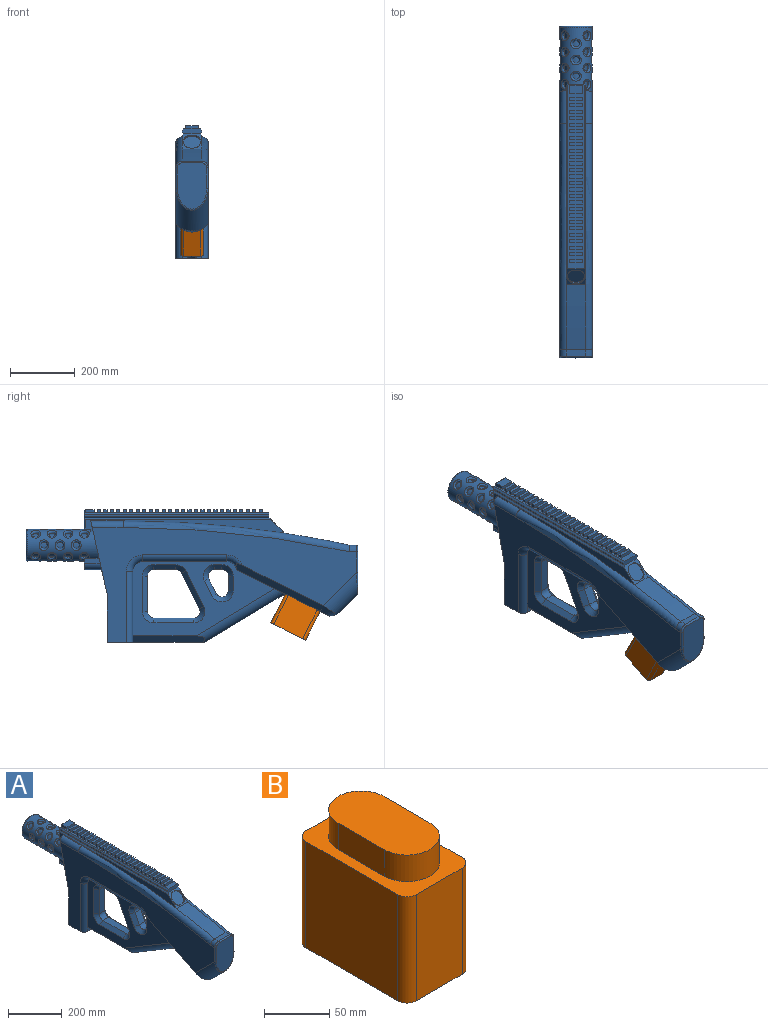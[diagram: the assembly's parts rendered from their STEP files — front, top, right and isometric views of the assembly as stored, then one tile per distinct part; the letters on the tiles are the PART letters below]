
ASSEMBLY  parts=2 mates=1
PART A: 340 faces, bbox 114x1061.1x421.4 mm
  f0: plane 168.93x84.47mm, normal (0,0.45,-0.89), area 4784.2mm2, adj f297,f298,f299,f300,f301,f303,f304,f307
  f1: plane 142.93x90mm, normal (0,-1,0), area 11537.9mm2, adj f308,f309,f310,f311,f312,f313
  f2: plane 60x47.7mm, normal (0,-0.71,0.71), area 1586.1mm2, adj f7,f8,f79,f80,f81,f82,f287,f288
  f3: plane 76.87x21.87mm, normal (0,0.98,-0.22), area 875.9mm2, adj f8,f13,f47,f225
  f4: plane 151.87x101.87mm, normal (0,0.98,-0.22), area 9786.5mm2, adj f9,f12,f13,f32,f33,f34,f87,f88
  f5: plane 567.11x50mm, normal (0,0,1), area 16871.1mm2, adj f82,f89,f90,f91,f92,f93,f94,f96
  f6: plane 60x20mm, normal (0,0,1), area 1200mm2, adj f44,f45,f79,f308
  f7: plane 614.81x42.7mm, normal (-1,0,0), area 8968mm2, adj f2,f15,f46,f48,f80,f225,f319,f325
  f8: plane 614.81x42.7mm, normal (1,0,0), area 8968mm2, adj f2,f3,f43,f47,f81,f225,f319,f320
  f9: plane 150x100mm, normal (0,1,0), area 15000mm2, adj f4,f12,f13,f14
  f10: plane 20x20mm, normal (0,-1,0), area 200mm2, adj f14,f38,f50
  f11: plane 20x20mm, normal (0,-1,0), area 200mm2, adj f14,f42,f49
  f12: plane 815.56x355mm, normal (-1,0,0), area 102541.9mm2, adj f4,f9,f14,f15,f39,f40,f41,f42
  f13: plane 815.56x355mm, normal (1,0,0), area 102541.9mm2, adj f3,f4,f9,f14,f35,f36,f37,f38
  f14: plane 305.72x105.72mm, normal (0,0,-1), area 12206.3mm2, adj f9,f10,f11,f12,f13,f38,f42,f49
  f15: plane 76.87x21.87mm, normal (0,0.98,-0.22), area 875.9mm2, adj f7,f12,f48,f225
  f16: plane 45.28x30mm, normal (0,-0.89,0.45), area 1518.7mm2, adj f25,f27,f71,f73
  f17: plane 45.28x30mm, normal (0,1,0), area 1358.4mm2, adj f25,f30,f70,f76
  f18: plane 122.64x30mm, normal (0,0,1), area 3679.2mm2, adj f26,f29,f58,f63
  f19: plane 110x55mm, normal (0,0.89,-0.45), area 3689.5mm2, adj f26,f31,f54,f59
  f20: plane 67.64x30mm, normal (0,0,-1), area 2029.2mm2, adj f28,f31,f51,f62
  f21: plane 30x22.64mm, normal (0,0,-1), area 679.2mm2, adj f27,f30,f67,f77
  f22: plane 110x30mm, normal (0,-1,0), area 3300mm2, adj f28,f29,f55,f66
  f23: plane 438.2x230mm, normal (1,0,0), area 38584.8mm2, adj f35,f36,f37,f38,f50,f59,f60,f61
  f24: plane 438.2x230mm, normal (-1,0,0), area 38584.8mm2, adj f39,f40,f41,f42,f49,f51,f52,f53
  f25: cylinder r=20mm len=37.89mm, axis (-1,0,0), area 1606.8mm2, adj f16,f17,f72,f74
  f26: cylinder r=20mm len=30mm, axis (1,0,0), area 1220.7mm2, adj f18,f19,f56,f61
  f27: cylinder r=20mm len=30mm, axis (1,0,0), area 1220.7mm2, adj f16,f21,f69,f75
  f28: cylinder r=20mm len=30mm, axis (1,0,0), area 942.5mm2, adj f20,f22,f53,f64
  f29: cylinder r=20mm len=30mm, axis (-1,0,0), area 942.5mm2, adj f18,f22,f57,f65
  f30: cylinder r=20mm len=30mm, axis (-1,0,0), area 942.5mm2, adj f17,f21,f68,f78
  f31: cylinder r=20mm len=30mm, axis (-1,0,0), area 664.3mm2, adj f19,f20,f52,f60
  f32: plane 48.89x15mm, normal (1,0,0), area 708.3mm2, adj f4,f87,f225,f316,f317
  f33: plane 48.89x15mm, normal (-1,0,0), area 708.3mm2, adj f4,f88,f225,f315,f317
  f34: plane 53.33x20mm, normal (0,0,-1), area 1066.7mm2, adj f4,f87,f88,f317
  f35: torus R=50mm, axis (1,0,0), area 1252mm2, adj f13,f23,f36,f297
  f36: cylinder r=20mm len=260.42mm, axis (0,-1,0), area 8181.3mm2, adj f13,f23,f35,f37
  f37: torus R=50mm, axis (1,0,0), area 1839.1mm2, adj f13,f23,f36,f38
  f38: cylinder r=20mm len=220mm, axis (0,0,1), area 6911.5mm2, adj f10,f13,f14,f23,f37
  f39: torus R=50mm, axis (1,0,0), area 1252.2mm2, adj f12,f24,f40,f299
  f40: cylinder r=20mm len=260.42mm, axis (0,1,0), area 8181.3mm2, adj f12,f24,f39,f41
  f41: torus R=50mm, axis (1,0,0), area 1839.1mm2, adj f12,f24,f40,f42
  f42: cylinder r=20mm len=220mm, axis (0,0,-1), area 6911.5mm2, adj f11,f12,f14,f24,f41
  f43: torus R=3284.17mm, axis (1,0,0), area 22144mm2, adj f8,f13,f44,f47,f79
  f44: cylinder r=20mm len=22.15mm, axis (0,1,0), area 662mm2, adj f6,f13,f43,f310
  f45: cylinder r=20mm len=22.15mm, axis (0,-1,0), area 662mm2, adj f6,f12,f46,f309
  f46: torus R=3284.17mm, axis (1,0,0), area 22144mm2, adj f7,f12,f45,f48,f79
  f47: cylinder r=20mm len=100mm, axis (0,-1,0), area 3071.8mm2, adj f3,f8,f13,f43
  f48: cylinder r=20mm len=100mm, axis (0,-1,0), area 3071.8mm2, adj f7,f12,f15,f46
  f49: plane 221.84x20mm, normal (-0.71,0,-0.71), area 6178.6mm2, adj f11,f14,f24,f307
  f50: plane 221.84x20mm, normal (0.71,0,-0.71), area 6178.6mm2, adj f10,f14,f23,f307
  f51: plane 67.64x15mm, normal (-0.71,0,-0.71), area 1434.8mm2, adj f20,f24,f52,f53
  f52: cone r=35mm half-angle=45deg, axis (-1,0,0), area 645.9mm2, adj f24,f31,f51,f54
  f53: cone r=35mm half-angle=45deg, axis (-1,0,0), area 916.3mm2, adj f24,f28,f51,f55
  f54: plane 116.71x68.42mm, normal (-0.71,0.63,-0.32), area 2608.9mm2, adj f19,f24,f52,f56
  f55: plane 110x15mm, normal (-0.71,-0.71,0), area 2333.5mm2, adj f22,f24,f53,f57
  f56: cone r=35mm half-angle=45deg, axis (-1,0,0), area 1186.8mm2, adj f24,f26,f54,f58
  f57: cone r=35mm half-angle=45deg, axis (-1,0,0), area 916.3mm2, adj f24,f29,f55,f58
  f58: plane 122.64x15mm, normal (-0.71,0,0.71), area 2601.6mm2, adj f18,f24,f56,f57
  f59: plane 116.71x68.42mm, normal (0.71,0.63,-0.32), area 2608.9mm2, adj f19,f23,f60,f61
  f60: cone r=35mm half-angle=45deg, axis (1,0,0), area 645.9mm2, adj f23,f31,f59,f62
  f61: cone r=35mm half-angle=45deg, axis (1,0,0), area 1186.8mm2, adj f23,f26,f59,f63
  f62: plane 67.64x15mm, normal (0.71,0,-0.71), area 1434.8mm2, adj f20,f23,f60,f64
  f63: plane 122.64x15mm, normal (0.71,0,0.71), area 2601.6mm2, adj f18,f23,f61,f65
  f64: cone r=35mm half-angle=45deg, axis (1,0,0), area 916.3mm2, adj f23,f28,f62,f66
  f65: cone r=35mm half-angle=45deg, axis (1,0,0), area 916.3mm2, adj f23,f29,f63,f66
  f66: plane 110x15mm, normal (0.71,-0.71,0), area 2333.5mm2, adj f22,f23,f64,f65
  f67: plane 22.64x15mm, normal (-0.71,0,-0.71), area 480.3mm2, adj f21,f24,f68,f69
  f68: cone r=35mm half-angle=45deg, axis (-1,0,0), area 916.3mm2, adj f24,f30,f67,f70
  f69: cone r=35mm half-angle=45deg, axis (-1,0,0), area 1186.8mm2, adj f24,f27,f67,f71
  f70: plane 45.28x15mm, normal (-0.71,0.71,0), area 960.5mm2, adj f17,f24,f68,f72
  f71: plane 51.99x36.06mm, normal (-0.71,-0.63,0.32), area 1073.9mm2, adj f16,f24,f69,f72
  f72: cone r=35mm half-angle=45deg, axis (-1,0,0), area 1562.2mm2, adj f24,f25,f70,f71
  f73: plane 51.99x36.06mm, normal (0.71,-0.63,0.32), area 1073.9mm2, adj f16,f23,f74,f75
  f74: cone r=35mm half-angle=45deg, axis (1,0,0), area 1562.2mm2, adj f23,f25,f73,f76
  f75: cone r=35mm half-angle=45deg, axis (1,0,0), area 1186.8mm2, adj f23,f27,f73,f77
  f76: plane 45.28x15mm, normal (0.71,0.71,0), area 960.5mm2, adj f17,f23,f74,f78
  f77: plane 22.64x15mm, normal (0.71,0,-0.71), area 480.3mm2, adj f21,f23,f75,f78
  f78: cone r=35mm half-angle=45deg, axis (1,0,0), area 916.3mm2, adj f23,f30,f76,f77
  f79: cylinder r=3304.17mm len=202.3mm, axis (-1,0,0), area 12344.7mm2, adj f2,f6,f43,f46
  f80: plane 572.11x5mm, normal (-0.71,0,0.71), area 4027.8mm2, adj f2,f7,f86,f332
  f81: plane 572.11x5mm, normal (0.71,0,0.71), area 4027.8mm2, adj f2,f8,f85,f322
  f82: plane 60x15mm, normal (0,-1,0), area 850mm2, adj f2,f5,f83,f84,f85,f86,f89,f90
  f83: plane 567.11x5mm, normal (1,0,0), area 2835.6mm2, adj f82,f85,f90,f327
  f84: plane 567.11x5mm, normal (-1,0,0), area 2835.6mm2, adj f82,f86,f89,f336
  f85: plane 567.11x5mm, normal (0.71,0,-0.71), area 4010.1mm2, adj f81,f82,f83,f324
  f86: plane 567.11x5mm, normal (-0.71,0,-0.71), area 4010.1mm2, adj f80,f82,f84,f334
  f87: cylinder r=20mm len=53.33mm, axis (0,-1,0), area 1605.7mm2, adj f4,f32,f34,f317
  f88: cylinder r=20mm len=53.33mm, axis (0,1,0), area 1605.7mm2, adj f4,f33,f34,f317
  f89: plane 567.11x5mm, normal (-0.71,0,0.71), area 4010.1mm2, adj f5,f82,f84,f338
  f90: plane 567.11x5mm, normal (0.71,0,0.71), area 4010.1mm2, adj f5,f82,f83,f329
  f91: plane 40x10mm, normal (0,-1,0), area 400mm2, adj f5,f92,f94,f95
  f92: plane 10x10mm, normal (1,0,0), area 100mm2, adj f5,f91,f93,f95
  f93: plane 40x10mm, normal (0,1,0), area 400mm2, adj f5,f92,f94,f95
  f94: plane 10x10mm, normal (-1,0,0), area 100mm2, adj f5,f91,f93,f95
  f95: plane 40x10mm, normal (0,0,1), area 400mm2, adj f91,f92,f93,f94
  f96: plane 10x10mm, normal (-1,0,0), area 100mm2, adj f5,f97,f99,f100
  f97: plane 40x10mm, normal (0,-1,0), area 400mm2, adj f5,f96,f98,f100
  f98: plane 10x10mm, normal (1,0,0), area 100mm2, adj f5,f97,f99,f100
  f99: plane 40x10mm, normal (0,1,0), area 400mm2, adj f5,f96,f98,f100
  f100: plane 40x10mm, normal (0,0,1), area 400mm2, adj f96,f97,f98,f99
  f101: plane 40x10mm, normal (0,-1,0), area 400mm2, adj f5,f102,f104,f105
  f102: plane 10x10mm, normal (1,0,0), area 100mm2, adj f5,f101,f103,f105
  f103: plane 40x10mm, normal (0,1,0), area 400mm2, adj f5,f102,f104,f105
  f104: plane 10x10mm, normal (-1,0,0), area 100mm2, adj f5,f101,f103,f105
  f105: plane 40x10mm, normal (0,0,1), area 400mm2, adj f101,f102,f103,f104
  f106: plane 40x10mm, normal (0,-1,0), area 400mm2, adj f5,f107,f109,f110
  f107: plane 10x10mm, normal (1,0,0), area 100mm2, adj f5,f106,f108,f110
  f108: plane 40x10mm, normal (0,1,0), area 400mm2, adj f5,f107,f109,f110
  f109: plane 10x10mm, normal (-1,0,0), area 100mm2, adj f5,f106,f108,f110
  f110: plane 40x10mm, normal (0,0,1), area 400mm2, adj f106,f107,f108,f109
  f111: plane 40x10mm, normal (0,-1,0), area 400mm2, adj f5,f112,f114,f115
  f112: plane 10x10mm, normal (1,0,0), area 100mm2, adj f5,f111,f113,f115
  f113: plane 40x10mm, normal (0,1,0), area 400mm2, adj f5,f112,f114,f115
  f114: plane 10x10mm, normal (-1,0,0), area 100mm2, adj f5,f111,f113,f115
  f115: plane 40x10mm, normal (0,0,1), area 400mm2, adj f111,f112,f113,f114
  f116: plane 40x10mm, normal (0,-1,0), area 400mm2, adj f5,f117,f119,f120
  f117: plane 10x10mm, normal (1,0,0), area 100mm2, adj f5,f116,f118,f120
  f118: plane 40x10mm, normal (0,1,0), area 400mm2, adj f5,f117,f119,f120
  f119: plane 10x10mm, normal (-1,0,0), area 100mm2, adj f5,f116,f118,f120
  f120: plane 40x10mm, normal (0,0,1), area 400mm2, adj f116,f117,f118,f119
  f121: plane 10x10mm, normal (-1,0,0), area 100mm2, adj f5,f122,f124,f125
  f122: plane 40x10mm, normal (0,-1,0), area 400mm2, adj f5,f121,f123,f125
  f123: plane 10x10mm, normal (1,0,0), area 100mm2, adj f5,f122,f124,f125
  f124: plane 40x10mm, normal (0,1,0), area 400mm2, adj f5,f121,f123,f125
  f125: plane 40x10mm, normal (0,0,1), area 400mm2, adj f121,f122,f123,f124
  f126: plane 40x10mm, normal (0,-1,0), area 400mm2, adj f5,f127,f129,f130
  f127: plane 10x10mm, normal (1,0,0), area 100mm2, adj f5,f126,f128,f130
  f128: plane 40x10mm, normal (0,1,0), area 400mm2, adj f5,f127,f129,f130
  f129: plane 10x10mm, normal (-1,0,0), area 100mm2, adj f5,f126,f128,f130
  f130: plane 40x10mm, normal (0,0,1), area 400mm2, adj f126,f127,f128,f129
  f131: plane 40x10mm, normal (0,-1,0), area 400mm2, adj f5,f132,f134,f135
  f132: plane 10x10mm, normal (1,0,0), area 100mm2, adj f5,f131,f133,f135
  f133: plane 40x10mm, normal (0,1,0), area 400mm2, adj f5,f132,f134,f135
  f134: plane 10x10mm, normal (-1,0,0), area 100mm2, adj f5,f131,f133,f135
  f135: plane 40x10mm, normal (0,0,1), area 400mm2, adj f131,f132,f133,f134
  f136: plane 40x10mm, normal (0,-1,0), area 400mm2, adj f5,f137,f139,f140
  f137: plane 10x10mm, normal (1,0,0), area 100mm2, adj f5,f136,f138,f140
  f138: plane 40x10mm, normal (0,1,0), area 400mm2, adj f5,f137,f139,f140
  f139: plane 10x10mm, normal (-1,0,0), area 100mm2, adj f5,f136,f138,f140
  f140: plane 40x10mm, normal (0,0,1), area 400mm2, adj f136,f137,f138,f139
  f141: plane 10x10mm, normal (-1,0,0), area 100mm2, adj f5,f142,f144,f145
  f142: plane 40x10mm, normal (0,-1,0), area 400mm2, adj f5,f141,f143,f145
  f143: plane 10x10mm, normal (1,0,0), area 100mm2, adj f5,f142,f144,f145
  f144: plane 40x10mm, normal (0,1,0), area 400mm2, adj f5,f141,f143,f145
  f145: plane 40x10mm, normal (0,0,1), area 400mm2, adj f141,f142,f143,f144
  f146: plane 40x10mm, normal (0,-1,0), area 400mm2, adj f5,f147,f149,f150
  f147: plane 10x10mm, normal (1,0,0), area 100mm2, adj f5,f146,f148,f150
  f148: plane 40x10mm, normal (0,1,0), area 400mm2, adj f5,f147,f149,f150
  f149: plane 10x10mm, normal (-1,0,0), area 100mm2, adj f5,f146,f148,f150
  f150: plane 40x10mm, normal (0,0,1), area 400mm2, adj f146,f147,f148,f149
  f151: plane 10x10mm, normal (-1,0,0), area 100mm2, adj f5,f152,f154,f155
  f152: plane 40x10mm, normal (0,-1,0), area 400mm2, adj f5,f151,f153,f155
  f153: plane 10x10mm, normal (1,0,0), area 100mm2, adj f5,f152,f154,f155
  f154: plane 40x10mm, normal (0,1,0), area 400mm2, adj f5,f151,f153,f155
  f155: plane 40x10mm, normal (0,0,1), area 400mm2, adj f151,f152,f153,f154
  f156: plane 10x10mm, normal (-1,0,0), area 100mm2, adj f5,f157,f159,f160
  f157: plane 40x10mm, normal (0,-1,0), area 400mm2, adj f5,f156,f158,f160
  f158: plane 10x10mm, normal (1,0,0), area 100mm2, adj f5,f157,f159,f160
  f159: plane 40x10mm, normal (0,1,0), area 400mm2, adj f5,f156,f158,f160
  f160: plane 40x10mm, normal (0,0,1), area 400mm2, adj f156,f157,f158,f159
  f161: plane 10x10mm, normal (-1,0,0), area 100mm2, adj f5,f162,f164,f165
  f162: plane 40x10mm, normal (0,-1,0), area 400mm2, adj f5,f161,f163,f165
  f163: plane 10x10mm, normal (1,0,0), area 100mm2, adj f5,f162,f164,f165
  f164: plane 40x10mm, normal (0,1,0), area 400mm2, adj f5,f161,f163,f165
  f165: plane 40x10mm, normal (0,0,1), area 400mm2, adj f161,f162,f163,f164
  f166: plane 10x10mm, normal (-1,0,0), area 100mm2, adj f5,f167,f169,f170
  f167: plane 40x10mm, normal (0,-1,0), area 400mm2, adj f5,f166,f168,f170
  f168: plane 10x10mm, normal (1,0,0), area 100mm2, adj f5,f167,f169,f170
  f169: plane 40x10mm, normal (0,1,0), area 400mm2, adj f5,f166,f168,f170
  f170: plane 40x10mm, normal (0,0,1), area 400mm2, adj f166,f167,f168,f169
  f171: plane 10x10mm, normal (-1,0,0), area 100mm2, adj f5,f172,f174,f175
  f172: plane 40x10mm, normal (0,-1,0), area 400mm2, adj f5,f171,f173,f175
  f173: plane 10x10mm, normal (1,0,0), area 100mm2, adj f5,f172,f174,f175
  f174: plane 40x10mm, normal (0,1,0), area 400mm2, adj f5,f171,f173,f175
  f175: plane 40x10mm, normal (0,0,1), area 400mm2, adj f171,f172,f173,f174
  f176: plane 10x10mm, normal (-1,0,0), area 100mm2, adj f5,f177,f179,f180
  f177: plane 40x10mm, normal (0,-1,0), area 400mm2, adj f5,f176,f178,f180
  f178: plane 10x10mm, normal (1,0,0), area 100mm2, adj f5,f177,f179,f180
  f179: plane 40x10mm, normal (0,1,0), area 400mm2, adj f5,f176,f178,f180
  f180: plane 40x10mm, normal (0,0,1), area 400mm2, adj f176,f177,f178,f179
  f181: plane 10x10mm, normal (-1,0,0), area 100mm2, adj f5,f182,f184,f185
  f182: plane 40x10mm, normal (0,-1,0), area 400mm2, adj f5,f181,f183,f185
  f183: plane 10x10mm, normal (1,0,0), area 100mm2, adj f5,f182,f184,f185
  f184: plane 40x10mm, normal (0,1,0), area 400mm2, adj f5,f181,f183,f185
  f185: plane 40x10mm, normal (0,0,1), area 400mm2, adj f181,f182,f183,f184
  f186: plane 10x10mm, normal (-1,0,0), area 100mm2, adj f5,f187,f189,f190
  f187: plane 40x10mm, normal (0,-1,0), area 400mm2, adj f5,f186,f188,f190
  f188: plane 10x10mm, normal (1,0,0), area 100mm2, adj f5,f187,f189,f190
  f189: plane 40x10mm, normal (0,1,0), area 400mm2, adj f5,f186,f188,f190
  f190: plane 40x10mm, normal (0,0,1), area 400mm2, adj f186,f187,f188,f189
  f191: plane 10x10mm, normal (-1,0,0), area 100mm2, adj f5,f192,f194,f195
  f192: plane 40x10mm, normal (0,-1,0), area 400mm2, adj f5,f191,f193,f195
  f193: plane 10x10mm, normal (1,0,0), area 100mm2, adj f5,f192,f194,f195
  f194: plane 40x10mm, normal (0,1,0), area 400mm2, adj f5,f191,f193,f195
  f195: plane 40x10mm, normal (0,0,1), area 400mm2, adj f191,f192,f193,f194
  f196: plane 10x10mm, normal (-1,0,0), area 100mm2, adj f5,f197,f199,f200
  f197: plane 40x10mm, normal (0,-1,0), area 400mm2, adj f5,f196,f198,f200
  f198: plane 10x10mm, normal (1,0,0), area 100mm2, adj f5,f197,f199,f200
  f199: plane 40x10mm, normal (0,1,0), area 400mm2, adj f5,f196,f198,f200
  f200: plane 40x10mm, normal (0,0,1), area 400mm2, adj f196,f197,f198,f199
  f201: plane 10x10mm, normal (-1,0,0), area 100mm2, adj f5,f202,f204,f205
  f202: plane 40x10mm, normal (0,-1,0), area 400mm2, adj f5,f201,f203,f205
  f203: plane 10x10mm, normal (1,0,0), area 100mm2, adj f5,f202,f204,f205
  f204: plane 40x10mm, normal (0,1,0), area 400mm2, adj f5,f201,f203,f205
  f205: plane 40x10mm, normal (0,0,1), area 400mm2, adj f201,f202,f203,f204
  f206: plane 10x10mm, normal (-1,0,0), area 100mm2, adj f5,f207,f209,f210
  f207: plane 40x10mm, normal (0,-1,0), area 400mm2, adj f5,f206,f208,f210
  f208: plane 10x10mm, normal (1,0,0), area 100mm2, adj f5,f207,f209,f210
  f209: plane 40x10mm, normal (0,1,0), area 400mm2, adj f5,f206,f208,f210
  f210: plane 40x10mm, normal (0,0,1), area 400mm2, adj f206,f207,f208,f209
  f211: plane 10x10mm, normal (-1,0,0), area 100mm2, adj f5,f212,f214,f215
  f212: plane 40x10mm, normal (0,-1,0), area 400mm2, adj f5,f211,f213,f215
  f213: plane 10x10mm, normal (1,0,0), area 100mm2, adj f5,f212,f214,f215
  f214: plane 40x10mm, normal (0,1,0), area 400mm2, adj f5,f211,f213,f215
  f215: plane 40x10mm, normal (0,0,1), area 400mm2, adj f211,f212,f213,f214
  f216: plane 40x10mm, normal (0,-1,0), area 400mm2, adj f5,f217,f218,f219
  f217: plane 27.11x10mm, normal (1,0,0), area 271.1mm2, adj f5,f216,f219,f333
  f218: plane 27.11x10mm, normal (-1,0,0), area 271.1mm2, adj f5,f216,f219,f337
  f219: plane 40x27.11mm, normal (0,0,1), area 1084.5mm2, adj f216,f217,f218,f335
  f220: plane 10x10mm, normal (1,0,0), area 100mm2, adj f5,f221,f223,f224
  f221: plane 40x10mm, normal (0,1,0), area 400mm2, adj f5,f220,f222,f224
  f222: plane 10x10mm, normal (-1,0,0), area 100mm2, adj f5,f221,f223,f224
  f223: plane 40x10mm, normal (0,-1,0), area 400mm2, adj f5,f220,f222,f224
  f224: plane 40x10mm, normal (0,0,1), area 400mm2, adj f220,f221,f222,f223
  f225: cylinder r=50mm len=220.56mm, axis (0,1,0), area 40915mm2, adj f3,f4,f7,f8,f15,f32,f33,f228
  f226: cylinder r=40mm len=195mm, axis (0,1,0), area 31299.6mm2, adj f227,f229,f231,f233,f235,f237,f239,f241
  f227: plane 80x80mm, normal (0,1,0), area 1178.1mm2, adj f226,f285
  f228: bspline ~30.01x23.58mm, area 668.6mm2, adj f225,f229
  f229: bspline ~29.98x19.83mm, area 508.6mm2, adj f226,f228
  f230: bspline ~30.01x23.58mm, area 668.6mm2, adj f225,f231
  f231: bspline ~29.98x19.83mm, area 508.6mm2, adj f226,f230
  f232: bspline ~30.01x23.58mm, area 668.6mm2, adj f225,f233
  f233: bspline ~29.98x19.83mm, area 508.6mm2, adj f226,f232
  f234: bspline ~30.01x23.58mm, area 668.6mm2, adj f225,f235
  f235: bspline ~29.98x19.83mm, area 508.6mm2, adj f226,f234
  f236: bspline ~33.35x30.01mm, area 668.6mm2, adj f225,f237
  f237: bspline ~29.98x26.65mm, area 508.6mm2, adj f226,f236
  f238: bspline ~33.35x30.01mm, area 668.6mm2, adj f225,f239
  f239: bspline ~29.98x26.65mm, area 508.6mm2, adj f226,f238
  f240: bspline ~33.35x30.01mm, area 668.6mm2, adj f225,f241
  f241: bspline ~29.98x26.65mm, area 508.6mm2, adj f226,f240
  f242: bspline ~33.35x30.01mm, area 668.8mm2, adj f225,f243
  f243: bspline ~29.98x26.65mm, area 508.6mm2, adj f226,f242
  f244: bspline ~33.35x30.01mm, area 668.8mm2, adj f225,f245
  f245: bspline ~29.98x26.65mm, area 508.6mm2, adj f226,f244
  f246: bspline ~33.35x30.01mm, area 668.8mm2, adj f225,f247
  f247: bspline ~29.98x26.65mm, area 508.6mm2, adj f226,f246
  f248: bspline ~33.35x30.01mm, area 668.6mm2, adj f225,f249
  f249: bspline ~29.98x26.65mm, area 508.6mm2, adj f226,f248
  f250: bspline ~33.35x30.01mm, area 668.6mm2, adj f225,f251
  f251: bspline ~29.98x26.65mm, area 508.6mm2, adj f226,f250
  f252: bspline ~33.35x30.01mm, area 668.6mm2, adj f225,f253
  f253: bspline ~29.98x26.65mm, area 508.6mm2, adj f226,f252
  f254: bspline ~33.35x30.01mm, area 668.6mm2, adj f225,f255
  f255: bspline ~29.98x26.65mm, area 508.6mm2, adj f226,f254
  f256: bspline ~33.35x30.01mm, area 668.6mm2, adj f225,f257
  f257: bspline ~29.98x26.65mm, area 508.6mm2, adj f226,f256
  f258: bspline ~33.35x30.01mm, area 668.6mm2, adj f225,f259
  f259: bspline ~29.98x26.65mm, area 508.6mm2, adj f226,f258
  f260: bspline ~30.01x23.58mm, area 668.6mm2, adj f225,f261
  f261: bspline ~29.98x19.83mm, area 508.6mm2, adj f226,f260
  f262: bspline ~30.01x23.58mm, area 668.6mm2, adj f225,f263
  f263: bspline ~29.98x19.83mm, area 508.6mm2, adj f226,f262
  f264: bspline ~30.01x23.58mm, area 668.6mm2, adj f225,f265
  f265: bspline ~29.98x19.83mm, area 508.6mm2, adj f226,f264
  f266: bspline ~30.01x23.58mm, area 668.6mm2, adj f225,f267,f316
  f267: bspline ~29.98x19.83mm, area 508.6mm2, adj f226,f266
  f268: bspline ~30.04x23.59mm, area 668.8mm2, adj f225,f269
  f269: bspline ~29.98x19.83mm, area 508.7mm2, adj f226,f268
  f270: bspline ~30.04x23.59mm, area 668.8mm2, adj f225,f271
  f271: bspline ~29.98x19.83mm, area 508.7mm2, adj f226,f270
  f272: bspline ~30.04x23.59mm, area 668.8mm2, adj f225,f273
  f273: bspline ~29.98x19.83mm, area 508.7mm2, adj f226,f272
  f274: bspline ~30.04x23.59mm, area 668.8mm2, adj f225,f275,f315
  f275: bspline ~29.98x19.83mm, area 508.7mm2, adj f226,f274
  f276: bspline ~30.04x23.59mm, area 668.8mm2, adj f225,f277
  f277: bspline ~29.98x19.83mm, area 508.7mm2, adj f226,f276
  f278: bspline ~30.04x23.59mm, area 668.8mm2, adj f225,f279
  f279: bspline ~29.98x19.83mm, area 508.7mm2, adj f226,f278
  f280: bspline ~30.04x23.59mm, area 668.8mm2, adj f225,f281
  f281: bspline ~29.98x19.83mm, area 508.7mm2, adj f226,f280
  f282: bspline ~30.04x23.59mm, area 668.8mm2, adj f225,f283
  f283: bspline ~29.98x19.83mm, area 508.7mm2, adj f226,f282
  f284: torus R=45mm, axis (0,1,0), area 4441.3mm2, adj f225,f226
  f285: cylinder r=35mm len=190mm, axis (0,-1,0), area 41783.2mm2, adj f227,f286
  f286: plane 70x70mm, normal (0,1,0), area 2591.8mm2, adj f285,f305
  f287: plane 10x3.54mm, normal (0,-0.71,-0.71), area 50mm2, adj f2,f291,f292,f295
  f288: plane 14.41x14.41mm, normal (1,0,0), area 76.9mm2, adj f2,f291,f292,f293
  f289: plane 10x3.54mm, normal (0,0.71,0.71), area 50mm2, adj f2,f291,f293,f294
  f290: plane 14.41x14.41mm, normal (-1,0,0), area 76.9mm2, adj f2,f291,f294,f295
  f291: plane 50x39.16mm, normal (0,-0.71,0.71), area 2425.9mm2, adj f287,f288,f289,f290,f292,f293,f294,f295
  f292: cylinder r=20mm len=20mm, axis (0,-0.71,0.71), area 157.1mm2, adj f2,f287,f288,f291
  f293: cylinder r=20mm len=20mm, axis (0,0.71,-0.71), area 157.1mm2, adj f2,f288,f289,f291
  f294: cylinder r=20mm len=20mm, axis (0,-0.71,0.71), area 157.1mm2, adj f2,f289,f290,f291
  f295: cylinder r=20mm len=20mm, axis (0,0.71,-0.71), area 157.1mm2, adj f2,f287,f290,f291
  f296: cylinder r=50mm len=137.59mm, axis (0,0.71,-0.71), area 18210.5mm2, adj f12,f13,f298,f313
  f297: plane 269.45x147.11mm, normal (0.71,0.32,-0.63), area 8313.4mm2, adj f0,f13,f23,f35,f298
  f298: bspline ~100.01x51.37mm, area 3219.1mm2, adj f0,f296,f297,f299
  f299: plane 269.45x147.11mm, normal (-0.71,0.32,-0.63), area 8314.7mm2, adj f0,f12,f24,f39,f298
  f300: plane 55.9x44.72mm, normal (1,0,0), area 1250mm2, adj f0,f302,f303,f304
  f301: plane 55.9x44.72mm, normal (-1,0,0), area 1250mm2, adj f0,f302,f303,f304
  f302: plane 89.44x50mm, normal (0,0.45,-0.89), area 4463.5mm2, adj f300,f301,f303,f304
  f303: cylinder r=25mm len=50mm, axis (0,0.45,-0.89), area 1963.5mm2, adj f0,f300,f301,f302
  f304: cylinder r=25mm len=50mm, axis (0,0.45,-0.89), area 1963.5mm2, adj f0,f300,f301,f302
  f305: cylinder r=20mm len=175mm, axis (0,1,0), area 21991.1mm2, adj f286,f306
  f306: plane 40x40mm, normal (0,1,0), area 1256.6mm2, adj f305
  f307: cylinder r=30mm len=275.03mm, axis (0,0.86,-0.51), area 26712.1mm2, adj f0,f14,f23,f24,f49,f50
  f308: cylinder r=5mm len=60mm, axis (1,0,0), area 471.2mm2, adj f1,f6,f309,f310
  f309: torus R=15mm, axis (0,1,0), area 224.3mm2, adj f1,f45,f308,f311
  f310: torus R=15mm, axis (0,1,0), area 224.3mm2, adj f1,f44,f308,f312
  f311: cylinder r=5mm len=64.29mm, axis (0,0,-1), area 504.9mm2, adj f1,f12,f309,f313
  f312: cylinder r=5mm len=64.29mm, axis (0,0,1), area 504.9mm2, adj f1,f13,f310,f313
  f313: bspline ~100x67.14mm, area 1000.4mm2, adj f1,f296,f311,f312
  f314: plane 57.21x54.23mm, normal (0,1,0), area 2590.4mm2, adj f321,f322,f324,f326,f327,f329,f330,f331
  f315: cylinder r=50mm len=13.58mm, axis (0,-1,0), area 96.1mm2, adj f33,f274,f317
  f316: cylinder r=50mm len=13.58mm, axis (0,-1,0), area 67.2mm2, adj f32,f266,f317
  f317: plane 60x35mm, normal (0,1,0), area 1519.6mm2, adj f32,f33,f34,f87,f88,f225,f315,f316
  f318: cylinder r=60mm len=51.74mm, axis (0,1,0), area 915.4mm2, adj f319,f320,f325,f326
  f319: plane 60x13.16mm, normal (0,1,0), area 243.9mm2, adj f7,f8,f225,f318,f320,f325
  f320: plane 17.11x4.13mm, normal (0.53,0,-0.85), area 83.6mm2, adj f8,f318,f319,f323
  f321: plane 30.1x2.89mm, normal (0.71,0.71,0), area 120.4mm2, adj f8,f314,f322,f323
  f322: plane 9.08x6.2mm, normal (0.5,0.71,0.5), area 32.3mm2, adj f81,f314,f321,f324
  f323: plane 4.13x2.89mm, normal (0.47,0.47,-0.75), area 8mm2, adj f320,f321,f326
  f324: plane 9.08x6.2mm, normal (0.5,0.71,-0.5), area 32.3mm2, adj f85,f314,f322,f327
  f325: plane 17.11x4.13mm, normal (-0.53,0,-0.85), area 83.6mm2, adj f7,f318,f319,f328
  f326: cone r=60mm half-angle=45deg, axis (0,1,0), area 223.6mm2, adj f314,f318,f323,f328
  f327: plane 5x2.89mm, normal (0.71,0.71,0), area 15.5mm2, adj f83,f314,f324,f329
  f328: plane 4.13x2.89mm, normal (-0.47,0.47,-0.75), area 8mm2, adj f325,f326,f330
  f329: plane 6.2x6.2mm, normal (0.5,0.71,0.5), area 24mm2, adj f90,f314,f327,f331
  f330: plane 30.1x2.89mm, normal (-0.71,0.71,0), area 120.4mm2, adj f7,f314,f328,f332
  f331: plane 7.89x2.89mm, normal (0,0.71,0.71), area 23.9mm2, adj f5,f314,f329,f333
  f332: plane 9.08x6.2mm, normal (-0.5,0.71,0.5), area 32.3mm2, adj f80,f314,f330,f334
  f333: plane 12.89x2.89mm, normal (0.71,0.71,0), area 40.8mm2, adj f217,f314,f331,f335
  f334: plane 9.08x6.2mm, normal (-0.5,0.71,-0.5), area 32.3mm2, adj f86,f314,f332,f336
  f335: plane 40x2.89mm, normal (0,0.71,0.71), area 151.5mm2, adj f219,f314,f333,f337
  f336: plane 5x2.89mm, normal (-0.71,0.71,0), area 15.5mm2, adj f84,f314,f334,f338
  f337: plane 12.89x2.89mm, normal (-0.71,0.71,0), area 40.8mm2, adj f218,f314,f335,f339
  f338: plane 6.2x6.2mm, normal (-0.5,0.71,0.5), area 24mm2, adj f89,f314,f336,f339
  f339: plane 7.89x2.89mm, normal (0,0.71,0.71), area 23.9mm2, adj f5,f314,f337,f338
PART B: 15 faces, bbox 70x120x125 mm
  f0: plane 50x25mm, normal (1,0,0), area 1250mm2, adj f2,f3,f9,f10
  f1: plane 50x25mm, normal (-1,0,0), area 1250mm2, adj f2,f3,f9,f10
  f2: plane 100x50mm, normal (0,0,1), area 4463.5mm2, adj f0,f1,f9,f10
  f3: plane 120x70mm, normal (0,0,1), area 3850.7mm2, adj f0,f1,f4,f5,f6,f7,f9,f10
  f4: plane 100x50mm, normal (0,-1,0), area 5000mm2, adj f3,f8,f11,f14
  f5: plane 100x100mm, normal (-1,0,0), area 10000mm2, adj f3,f8,f11,f12
  f6: plane 100x50mm, normal (0,1,0), area 5000mm2, adj f3,f8,f12,f13
  f7: plane 100x100mm, normal (1,0,0), area 10000mm2, adj f3,f8,f13,f14
  f8: plane 120x70mm, normal (0,0,-1), area 8314.2mm2, adj f4,f5,f6,f7,f11,f12,f13,f14
  f9: cylinder r=25mm len=50mm, axis (0,0,-1), area 1963.5mm2, adj f0,f1,f2,f3
  f10: cylinder r=25mm len=50mm, axis (0,0,1), area 1963.5mm2, adj f0,f1,f2,f3
  f11: cylinder r=10mm len=100mm, axis (0,0,-1), area 1570.8mm2, adj f3,f4,f5,f8
  f12: cylinder r=10mm len=100mm, axis (0,0,1), area 1570.8mm2, adj f3,f5,f6,f8
  f13: cylinder r=10mm len=100mm, axis (0,0,-1), area 1570.8mm2, adj f3,f6,f7,f8
  f14: cylinder r=10mm len=100mm, axis (0,0,1), area 1570.8mm2, adj f3,f4,f7,f8
PLACE A t=(-42.82,130.21,232.39)mm fixed
PLACE B rot(axis=(1,0,0),26.6deg) t=(-12.82,-174.2,205.19)mm
MATE fastened B.f2 <-> A.f302  axis (0,-0.45,0.89) through (-12.82,-185.39,227.55)mm
